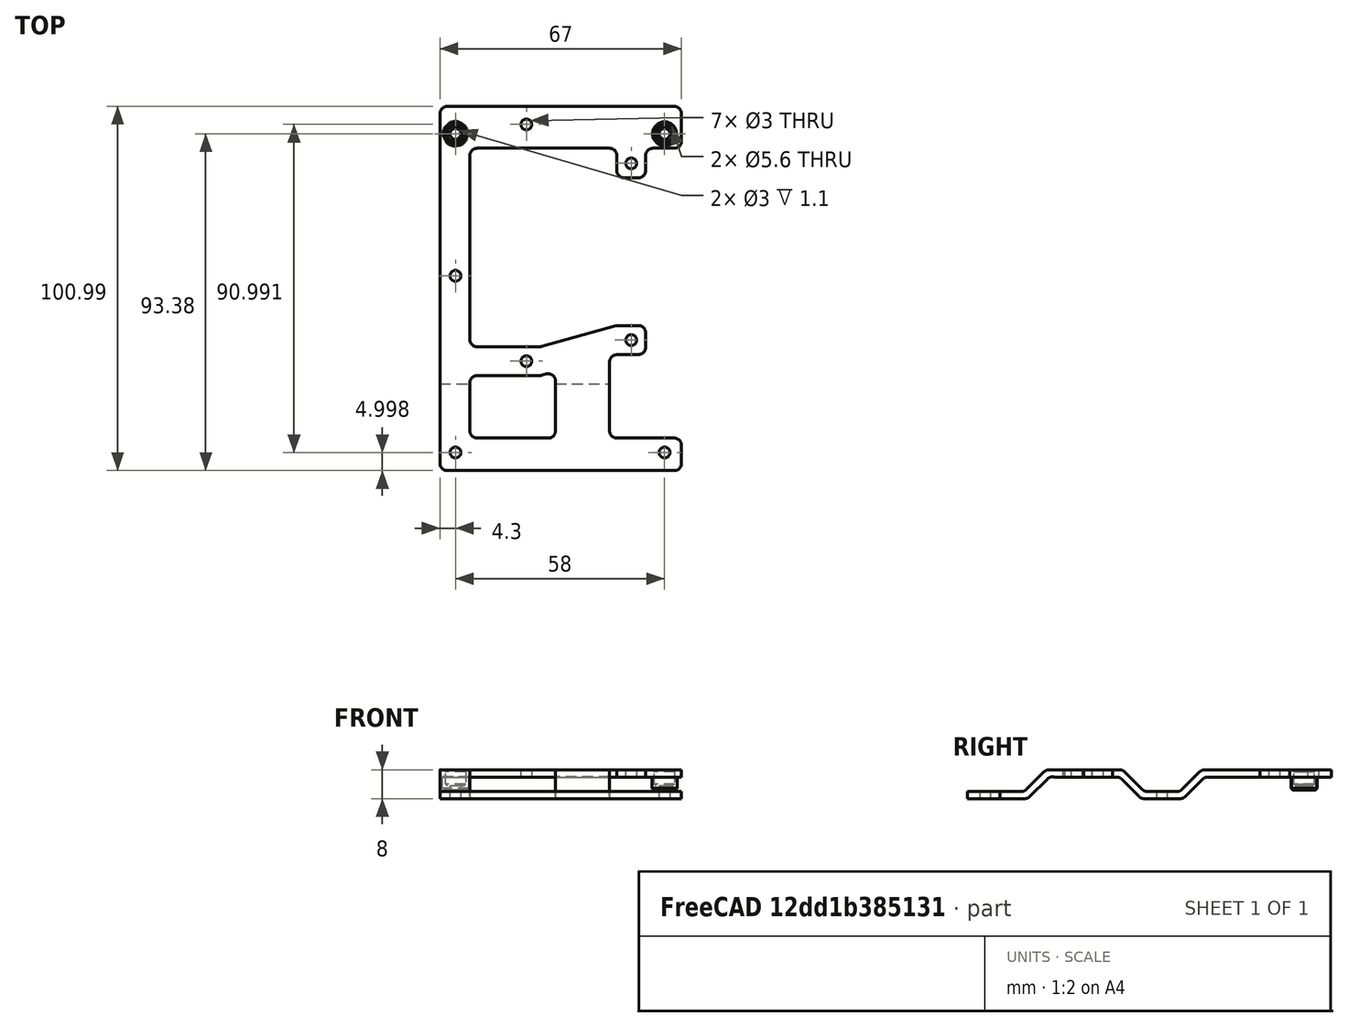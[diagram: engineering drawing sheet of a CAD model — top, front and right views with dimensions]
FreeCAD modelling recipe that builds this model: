
FCSTD DOCUMENT  (FreeCAD 0.18R15619 (Git))
Label: to-print-pi
License: All rights reserved
LicenseURL: http://en.wikipedia.org/wiki/All_rights_reserved
objects: Sketcher::SketchObject×5, PartDesign::Pad×2, PartDesign::Pocket×2, Mesh::Feature×1, PartDesign::Chamfer×1, PartDesign::Fillet×1, PartDesign::Body×1
note: 16 computed .brp shape members not serialized (recipe doc carries the construction recipe); baked Part::Feature solids carry a one-line shape summary decoded from their .brp

FEATURE [Mesh::Feature] temp
  Placement = pos=(56,-7,9.4) rot=(0,0,1;0rad)
FEATURE [Sketcher::SketchObject] Sketch004  label="sk-reference"
  MapMode = 5
  Support = -> [XY_Plane]
  sketch-geometry (9):
    g0: LineSegment StartX=-8.52936 StartY=35.1093 StartZ=0 EndX=20.5706 EndY=24.3093 EndZ=0
    g1: LineSegment StartX=20.5706 StartY=-24.6907 StartZ=0 EndX=-8.52936 EndY=-30.5407 EndZ=0
    g2: LineSegment StartX=29.8 StartY=-55.8821 StartZ=0 EndX=-28.2 EndY=-55.8821 EndZ=0
    g3: LineSegment StartX=-28.2 StartY=-55.8821 StartZ=0 EndX=-28.2 EndY=-6.88212 EndZ=0
    g4: LineSegment StartX=-28.2 StartY=32.5 StartZ=0 EndX=29.8 EndY=32.5 EndZ=0
    g5: LineSegment StartX=-8.52936 StartY=35.1093 StartZ=0 EndX=-8.52936 EndY=-30.5407 EndZ=0
    g6: LineSegment [constr] StartX=20.5706 StartY=24.3093 StartZ=0 EndX=20.5706 EndY=-24.6907 EndZ=0
    g7: LineSegment [constr] StartX=-28.2 StartY=32.5 StartZ=0 EndX=-28.2 EndY=-6.88212 EndZ=0
    g8: LineSegment [constr] StartX=29.8 StartY=32.5 StartZ=0 EndX=29.8 EndY=-55.8821 EndZ=0
  constraints (24):
    c: Horizontal(g2)
    c: Coincident(g2,g3)
    c: Vertical(g3)
    c: Horizontal(g4)
    c: Vertical(g5)
    c: Coincident(g1,g5)
    c: Coincident(g0,g5)
    c: DistanceX(g0,g0) = 29.1
    c: Distance(g5) = 65.65
    c: DistanceY(g1,g0) = 49
    c: DistanceY(g0,g0) = 10.8
    c: Vertical(g6)
    c: Coincident(g0,g6)
    c: Coincident(g1,g6)
    c: Equal(g2,g4)
    c: DistanceY(g-1,g4) = 32.5
    c: Coincident(g4,g7)
    c: Coincident(g3,g7)
    c: Vertical(g7)
    c: DistanceX(g4,g4) = 58
    c: Coincident(g4,g8)
    c: Coincident(g2,g8)
    c: Distance(g3) = 49
    c: DistanceX(g-2,g4) = -28.2
FEATURE [Sketcher::SketchObject] Sketch  label="sk-profile"
  ExternalGeometry = -> [Sketch004]
  MapMode = 5
  Placement = pos=(0,0,0) rot=(0.57735,0.57735,0.57735;2.0944rad)
  Support = -> [YZ_Plane]
  sketch-geometry (33):
    g0: LineSegment StartX=-38.7431 StartY=-2.51783 StartZ=0 EndX=-43.6395 EndY=-7.41421 EndZ=0
    g1: LineSegment StartX=-45.0537 StartY=-8 StartZ=0 EndX=-60.8821 EndY=-8 EndZ=0
    g2: LineSegment StartX=-60.8821 StartY=-8 StartZ=0 EndX=-60.8821 EndY=-6 EndZ=0
    g3: LineSegment StartX=-60.8821 StartY=-6 StartZ=0 EndX=-45.8821 EndY=-6 EndZ=0
    g4: LineSegment StartX=-44.4679 StartY=-5.41421 StartZ=0 EndX=-39.6395 EndY=-0.585786 EndZ=0
    g5: LineSegment StartX=40.1093 StartY=0 StartZ=0 EndX=40.1093 EndY=-2 EndZ=0
    g6: LineSegment [constr] StartX=-40.1573 StartY=-1.10362 StartZ=0 EndX=-38.7431 EndY=-2.51783 EndZ=0
    g7: ArcOfCircle CenterX=-37.3289 CenterY=-3.93205 CenterZ=0 NormalX=0 NormalY=0 NormalZ=1 AngleXU=0 Radius=2 StartAngle=1.30938 EndAngle=2.35619
    g8: ArcOfCircle CenterX=-38.2253 CenterY=-2 CenterZ=0 NormalX=0 NormalY=0 NormalZ=1 AngleXU=0 Radius=2 StartAngle=1.5708 EndAngle=2.35619
    g9: ArcOfCircle CenterX=-45.0537 CenterY=-6 CenterZ=0 NormalX=0 NormalY=0 NormalZ=1 AngleXU=0 Radius=2 StartAngle=4.71239 EndAngle=5.49779
    g10: ArcOfCircle CenterX=-45.8821 CenterY=-4 CenterZ=0 NormalX=0 NormalY=0 NormalZ=1 AngleXU=0 Radius=2 StartAngle=4.71239 EndAngle=5.49779
    g11: LineSegment StartX=-38.2253 StartY=0 StartZ=0 EndX=-18.7106 EndY=0 EndZ=0
    g12: LineSegment StartX=-17.2963 StartY=-0.585786 StartZ=0 EndX=-12.4679 EndY=-5.41421 EndZ=0
    g13: LineSegment StartX=-11.0537 StartY=-6 StartZ=0 EndX=-2.71055 EndY=-6 EndZ=0
    g14: LineSegment StartX=-1.29634 StartY=-5.41421 StartZ=0 EndX=3.53209 EndY=-0.585786 EndZ=0
    g15: LineSegment StartX=4.9463 StartY=0 StartZ=0 EndX=40.1093 EndY=0 EndZ=0
    g16: LineSegment StartX=40.1093 StartY=-2 StartZ=0 EndX=5.77473 EndY=-2 EndZ=0
    g17: LineSegment StartX=4.36052 StartY=-2.58579 StartZ=0 EndX=-0.46791 EndY=-7.41421 EndZ=0
    g18: LineSegment StartX=-1.88212 StartY=-8 StartZ=0 EndX=-11.8821 EndY=-8 EndZ=0
    g19: LineSegment StartX=-13.2963 StartY=-7.41421 StartZ=0 EndX=-18.1248 EndY=-2.58579 EndZ=0
    g20: LineSegment StartX=-19.539 StartY=-2 StartZ=0 EndX=-36.812 EndY=-2 EndZ=0
    g21: LineSegment [constr] StartX=-3.04361 StartY=-6 StartZ=0 EndX=-3.04361 EndY=-8 EndZ=0
    g22: LineSegment [constr] StartX=-21.0313 StartY=0 StartZ=0 EndX=-21.0313 EndY=-2 EndZ=0
    g23: LineSegment [constr] StartX=-15.0824 StartY=-5.62813 StartZ=0 EndX=-13.6682 EndY=-4.21391 EndZ=0
    g24: LineSegment [constr] StartX=2.2372 StartY=-1.88068 StartZ=0 EndX=3.65141 EndY=-3.29489 EndZ=0
    g25: ArcOfCircle CenterX=-2.71055 CenterY=-4 CenterZ=0 NormalX=0 NormalY=0 NormalZ=1 AngleXU=0 Radius=2 StartAngle=4.71239 EndAngle=5.49779
    g26: ArcOfCircle CenterX=-1.88212 CenterY=-6 CenterZ=0 NormalX=0 NormalY=0 NormalZ=1 AngleXU=0 Radius=2 StartAngle=4.71239 EndAngle=5.49779
    g27: ArcOfCircle CenterX=5.77473 CenterY=-4 CenterZ=0 NormalX=0 NormalY=0 NormalZ=1 AngleXU=0 Radius=2 StartAngle=1.5708 EndAngle=2.35619
    g28: ArcOfCircle CenterX=4.9463 CenterY=-2 CenterZ=0 NormalX=0 NormalY=0 NormalZ=1 AngleXU=0 Radius=2 StartAngle=1.5708 EndAngle=2.35619
    g29: ArcOfCircle CenterX=-11.0537 CenterY=-4 CenterZ=0 NormalX=0 NormalY=0 NormalZ=1 AngleXU=0 Radius=2 StartAngle=3.92699 EndAngle=4.71239
    g30: ArcOfCircle CenterX=-11.8821 CenterY=-6 CenterZ=0 NormalX=0 NormalY=0 NormalZ=1 AngleXU=0 Radius=2 StartAngle=3.92699 EndAngle=4.71239
    g31: ArcOfCircle CenterX=-19.539 CenterY=-4 CenterZ=0 NormalX=0 NormalY=0 NormalZ=1 AngleXU=0 Radius=2 StartAngle=0.785398 EndAngle=1.5708
    g32: ArcOfCircle CenterX=-18.7106 CenterY=-2 CenterZ=0 NormalX=0 NormalY=0 NormalZ=1 AngleXU=0 Radius=2 StartAngle=0.785398 EndAngle=1.5708
  constraints (87):
    c: Coincident(g1,g2)
    c: Coincident(g2,g3)
    c: Parallel(g3,g1)
    c: Parallel(g0,g4)
    c: Parallel(g2,g5)
    c: Perpendicular(g3,g2)
    c: Equal(g2,g5)
    c: Distance(g5) = 2
    c: Angle(g0,g-2) = 0.785398
    c: DistanceY(g-1,g1) = -8
    c: PointOnObject(g6,g4)
    c: Perpendicular(g0,g6)
    c: Equal(g6,g2)
    c: Tangent(g0,g7) = -1.5708
    c: Tangent(g4,g8) = 1.5708
    c: Tangent(g0,g9) = 1.5708
    c: Tangent(g1,g9) = 1.5708
    c: Tangent(g3,g10) = -1.5708
    c: Tangent(g4,g10) = -1.5708
    c: Equal(g9,g10)
    c: Equal(g10,g7)
    c: Equal(g7,g8)
    c: Radius(g7) = 2
    c: Distance(g3) = 15
    c: Coincident(g6,g0)
    c: Coincident(g8,g11)
    c: Coincident(g7,g20)
    c: Horizontal(g11)
    c: Horizontal(g20)
    c: Horizontal(g13)
    c: Horizontal(g18)
    c: Parallel(g12,g19)
    c: Parallel(g14,g17)
    c: Horizontal(g15)
    c: Horizontal(g16)
    c: Coincident(g15,g5)
    c: Coincident(g16,g5)
    c: Horizontal(g1,g18)
    c: PointOnObject(g21,g13)
    c: PointOnObject(g21,g18)
    c: Perpendicular(g18,g21)
    c: Equal(g21,g2)
    c: Perpendicular(g5,g15)
    c: PointOnObject(g22,g11)
    c: PointOnObject(g22,g20)
    c: Perpendicular(g20,g22)
    c: PointOnObject(g23,g12)
    c: PointOnObject(g23,g19)
    c: Perpendicular(g12,g23)
    c: Equal(g22,g23)
    c: Equal(g23,g6)
    c: PointOnObject(g24,g14)
    c: PointOnObject(g24,g17)
    c: Perpendicular(g17,g24)
    c: Equal(g24,g21)
    c: Angle(g-2,g12) = 0.785398
    c: Angle(g14,g-2) = 0.785398
    c: Tangent(g13,g25) = -1.5708
    c: Tangent(g14,g25) = -1.5708
    c: Tangent(g17,g26) = 1.5708
    c: Tangent(g18,g26) = 1.5708
    c: Tangent(g16,g27) = -1.5708
    c: Tangent(g17,g27) = -1.5708
    c: Tangent(g14,g28) = 1.5708
    c: Tangent(g15,g28) = 1.5708
    c: Tangent(g12,g29) = -1.5708
    c: Tangent(g13,g29) = -1.5708
    c: Tangent(g18,g30) = 1.5708
    c: Tangent(g19,g30) = 1.5708
    c: Tangent(g19,g31) = -1.5708
    c: Tangent(g20,g31) = -1.5708
    c: Tangent(g11,g32) = 1.5708
    c: Tangent(g12,g32) = 1.5708
    c: Equal(g31,g32)
    c: Equal(g32,g29)
    c: Equal(g29,g30)
    c: Equal(g30,g26)
    c: Equal(g26,g25)
    c: Equal(g25,g27)
    c: Equal(g27,g28)
    c: Equal(g28,g7)
    c: PointOnObject(g15,g-1)
    c: PointOnObject(g22,g-1)
    c: DistanceX(g-5,g5) = 5
    c: DistanceX(g2,g-3) = 5
    c: DistanceX(g-6,g26) = 5
    c: DistanceX(g30,g-6) = 5
FEATURE [PartDesign::Pad] Pad
  Length = 34.5
  Length2 = 32.5
  Placement = pos=(0,0,0) rot=(0.57735,0.57735,0.57735;2.0944rad)
  Profile = -> Sketch
  Type = 4
FEATURE [Sketcher::SketchObject] Sketch001
  ExternalGeometry = -> [Sketch004]
  MapMode = 5
  Support = -> [XY_Plane]
  sketch-geometry (32):
    g0: LineSegment StartX=-24.2 StartY=28.5 StartZ=0 EndX=16.5706 EndY=28.5 EndZ=0
    g1: LineSegment StartX=16.5706 StartY=-20.6907 StartZ=0 EndX=-4.52936 EndY=-26.5407 EndZ=0
    g2: LineSegment StartX=-4.52936 StartY=-26.5407 StartZ=0 EndX=-24.2 EndY=-26.5407 EndZ=0
    g3: LineSegment StartX=-24.2 StartY=-34.5407 StartZ=0 EndX=-4.52936 EndY=-34.5407 EndZ=0
    g4: LineSegment StartX=-24.2 StartY=28.5 StartZ=0 EndX=-24.2 EndY=-26.5407 EndZ=0
    g5: LineSegment StartX=-24.2 StartY=-34.5407 StartZ=0 EndX=-24.2 EndY=-51.8821 EndZ=0
    g6: LineSegment [constr] StartX=-18.9916 StartY=-26.5407 StartZ=0 EndX=-18.9916 EndY=-34.5407 EndZ=0
    g7: LineSegment StartX=24.5706 StartY=-20.6907 StartZ=0 EndX=24.5706 EndY=-28.6907 EndZ=0
    g8: LineSegment StartX=16.5706 StartY=28.5 StartZ=0 EndX=16.5706 EndY=20.3093 EndZ=0
    g9: LineSegment StartX=43.8761 StartY=28.5 StartZ=0 EndX=43.8761 EndY=-51.8821 EndZ=0
    g10: Circle CenterX=20.5706 CenterY=24.3093 CenterZ=0 NormalX=0 NormalY=0 NormalZ=1 AngleXU=0 Radius=1.5
    g11: Circle CenterX=-8.52936 CenterY=35.1093 CenterZ=0 NormalX=0 NormalY=0 NormalZ=1 AngleXU=0 Radius=1.5
    g12: Circle CenterX=20.5706 CenterY=-24.6907 CenterZ=0 NormalX=0 NormalY=0 NormalZ=1 AngleXU=0 Radius=1.5
    g13: Circle CenterX=-8.52936 CenterY=-30.5407 CenterZ=0 NormalX=0 NormalY=0 NormalZ=1 AngleXU=0 Radius=1.5
    g14: Circle CenterX=-28.2 CenterY=-55.8821 CenterZ=0 NormalX=0 NormalY=0 NormalZ=1 AngleXU=0 Radius=1.5
    g15: Circle CenterX=29.8 CenterY=-55.8821 CenterZ=0 NormalX=0 NormalY=0 NormalZ=1 AngleXU=0 Radius=1.5
    g16: LineSegment StartX=16.5706 StartY=20.3093 StartZ=0 EndX=24.5706 EndY=20.3093 EndZ=0
    g17: LineSegment StartX=24.5706 StartY=20.3093 StartZ=0 EndX=24.5706 EndY=28.5 EndZ=0
    g18: LineSegment StartX=24.5706 StartY=28.5 StartZ=0 EndX=43.8761 EndY=28.5 EndZ=0
    g19: LineSegment StartX=16.5706 StartY=-28.6907 StartZ=0 EndX=14.5488 EndY=-29.2512 EndZ=0
    g20: LineSegment StartX=14.5488 StartY=-29.2512 StartZ=0 EndX=14.5488 EndY=-51.8821 EndZ=0
    g21: LineSegment StartX=14.5488 StartY=-51.8821 StartZ=0 EndX=43.8761 EndY=-51.8821 EndZ=0
    g22: LineSegment StartX=-4.52936 StartY=-34.5407 StartZ=0 EndX=-0.451219 EndY=-33.41 EndZ=0
    g23: LineSegment StartX=-0.451219 StartY=-33.41 StartZ=0 EndX=-0.451219 EndY=-51.8821 EndZ=0
    g24: LineSegment StartX=-0.451219 StartY=-51.8821 StartZ=0 EndX=-24.2 EndY=-51.8821 EndZ=0
    g25: LineSegment [constr] StartX=-4.52936 StartY=-34.5407 StartZ=0 EndX=16.5706 EndY=-28.6907 EndZ=0
    g26: LineSegment StartX=16.5706 StartY=-20.6907 StartZ=0 EndX=24.5706 EndY=-20.6907 EndZ=0
    g27: LineSegment StartX=16.5706 StartY=-28.6907 StartZ=0 EndX=24.5706 EndY=-28.6907 EndZ=0
    g28: Circle CenterX=-28.2 CenterY=-6.88212 CenterZ=0 NormalX=0 NormalY=0 NormalZ=1 AngleXU=0 Radius=1.5
    g29: LineSegment [constr] StartX=-4.52936 StartY=-26.5407 StartZ=0 EndX=-4.52936 EndY=-34.5407 EndZ=0
    g30: LineSegment [constr] StartX=16.5706 StartY=-20.6907 StartZ=0 EndX=16.5706 EndY=-28.6907 EndZ=0
    g31: LineSegment [constr] StartX=16.5706 StartY=28.5 StartZ=0 EndX=24.5706 EndY=28.5 EndZ=0
  constraints (83):
    c: Horizontal(g0)
    c: Coincident(g1,g2)
    c: Coincident(g0,g4)
    c: Coincident(g2,g4)
    c: Coincident(g5,g3)
    c: Vertical(g4)
    c: Vertical(g5)
    c: Vertical(g3,g2)
    c: Vertical(g3,g1)
    c: PointOnObject(g6,g2)
    c: PointOnObject(g6,g3)
    c: Perpendicular(g2,g6)
    c: Perpendicular(g3,g6)
    c: Perpendicular(g5,g3)
    c: Equal(g7,g6)
    c: Vertical(g9)
    c: Coincident(g8,g0)
    c: Vertical(g8)
    c: Radius(g13) = 1.5
    c: Equal(g13,g12)
    c: Equal(g13,g10)
    c: Equal(g13,g11)
    c: Equal(g14,g13)
    c: Equal(g15,g13)
    c: Coincident(g16,g17)
    c: Coincident(g17,g18)
    c: Coincident(g9,g18)
    c: Vertical(g17)
    c: Horizontal(g18)
    c: Coincident(g16,g8)
    c: Horizontal(g16)
    c: Coincident(g19,g20)
    c: Coincident(g20,g21)
    c: Coincident(g22,g23)
    c: Coincident(g23,g24)
    c: Horizontal(g21)
    c: Horizontal(g24)
    c: Horizontal(g23,g20)
    c: Coincident(g24,g5)
    c: Coincident(g22,g3)
    c: Coincident(g25,g3)
    c: Parallel(g25,g1)
    c: PointOnObject(g19,g25)
    c: PointOnObject(g22,g25)
    c: Vertical(g20)
    c: Vertical(g23)
    c: Coincident(g9,g21)
    c: Coincident(g26,g1)
    c: Coincident(g26,g7)
    c: Vertical(g7)
    c: Coincident(g7,g27)
    c: Coincident(g19,g27)
    c: Coincident(g25,g19)
    c: Horizontal(g27)
    c: Horizontal(g26)
    c: Equal(g28,g14)
    c: Coincident(g10,g-5)
    c: Coincident(g11,g-5)
    c: Coincident(g13,g-7)
    c: Coincident(g12,g-7)
    c: Distance(g12,g26) = 4
    c: Distance(g12,g7) = 4
    c: Distance(g13,g2) = 4
    c: Distance(g6) = 8
    c: Distance(g5,g-9) = 4
    c: Distance(g5,g-8) = 4
    c: Coincident(g29,g1)
    c: Coincident(g29,g3)
    c: Distance(g13,g29) = 4
    c: Coincident(g19,g30)
    c: Coincident(g1,g30)
    c: Distance(g12,g30) = 4
    c: Distance(g23,g20) = 15
    c: Distance(g0,g-10) = 4
    c: Coincident(g0,g31)
    c: Coincident(g17,g31)
    c: Horizontal(g31)
    c: Distance(g10,g17) = 4
    c: Distance(g10,g8) = 4
    c: Distance(g10,g16) = 4
    c: Coincident(g28,g-8)
    c: Coincident(g14,g-9)
    c: Coincident(g15,g-9)
FEATURE [PartDesign::Pocket] Pocket
  BaseFeature = -> Pad
  Length = 5
  Length2 = 100
  Placement = pos=(0,0,0) rot=(0.57735,0.57735,0.57735;2.0944rad)
  Profile = -> Sketch001
  Type = 1
FEATURE [Sketcher::SketchObject] Sketch002
  ExternalGeometry = -> [Sketch004]
  MapMode = 5
  Support = -> [XY_Plane]
  sketch-geometry (4):
    g0: Circle CenterX=29.8 CenterY=32.5 CenterZ=0 NormalX=0 NormalY=0 NormalZ=1 AngleXU=0 Radius=3.5
    g1: Circle CenterX=29.8 CenterY=32.5 CenterZ=0 NormalX=0 NormalY=0 NormalZ=1 AngleXU=0 Radius=1.5
    g2: Circle CenterX=-28.2 CenterY=32.5 CenterZ=0 NormalX=0 NormalY=0 NormalZ=1 AngleXU=0 Radius=3.64545
    g3: Circle CenterX=-28.2 CenterY=32.5 CenterZ=0 NormalX=0 NormalY=0 NormalZ=1 AngleXU=0 Radius=1.5
  constraints (7):
    c: Coincident(g3,g2)
    c: Coincident(g1,g0)
    c: Radius(g1) = 1.5
    c: Equal(g1,g3)
    c: Radius(g0) = 3.5
    c: Coincident(g0,g-3)
    c: Coincident(g2,g-3)
FEATURE [PartDesign::Pad] Pad001
  BaseFeature = -> Pocket
  Length = 5.6
  Length2 = 100
  Placement = pos=(0,0,0) rot=(0.57735,0.57735,0.57735;2.0944rad)
  Profile = -> Sketch002
  Reversed = true
  Type = 0
FEATURE [Sketcher::SketchObject] Sketch003
  ExternalGeometry = -> [Sketch002]
  MapMode = 5
  Support = -> [XY_Plane]
  sketch-geometry (2):
    g0: Circle CenterX=-28.2 CenterY=32.5 CenterZ=0 NormalX=0 NormalY=0 NormalZ=1 AngleXU=0 Radius=2.8
    g1: Circle CenterX=29.8 CenterY=32.5 CenterZ=0 NormalX=0 NormalY=0 NormalZ=1 AngleXU=0 Radius=2.8
  constraints (4):
    c: Coincident(g1,g-4)
    c: Coincident(g0,g-3)
    c: Radius(g0) = 2.8
    c: Equal(g0,g1)
FEATURE [PartDesign::Pocket] Pocket001
  BaseFeature = -> Pad001
  Length = 4.5
  Length2 = 100
  Placement = pos=(0,0,0) rot=(0.57735,0.57735,0.57735;2.0944rad)
  Profile = -> Sketch003
  Type = 0
FEATURE [PartDesign::Chamfer] Chamfer
  Base = -> Pocket001 [Edge192,Edge194,Edge197,Edge199,Edge201,Edge203]
  BaseFeature = -> Pocket001
  Placement = pos=(0,0,0) rot=(0.57735,0.57735,0.57735;2.0944rad)
  Size = 0.5
FEATURE [PartDesign::Fillet] Fillet
  Base = -> Chamfer [Edge40,Edge50,Edge75,Edge194,Edge198,Edge179,Edge27,Edge58,Edge193,Edge70,Edge78,Edge122,Edge188,Edge172,Edge68,Edge74,Edge173,Edge175,Edge71,Edge174,Edge168,Edge195,Edge191]
  BaseFeature = -> Chamfer
  Placement = pos=(0,0,0) rot=(0.57735,0.57735,0.57735;2.0944rad)
  Radius = 2
FEATURE [PartDesign::Body] Body  label="plaque"
  Group = -> [Sketch,Sketch004,Pad,Sketch001,Pocket,Sketch002,Pad001,Sketch003,Pocket001,Chamfer,Fillet]
  Origin = -> Origin
  Tip = -> Fillet
